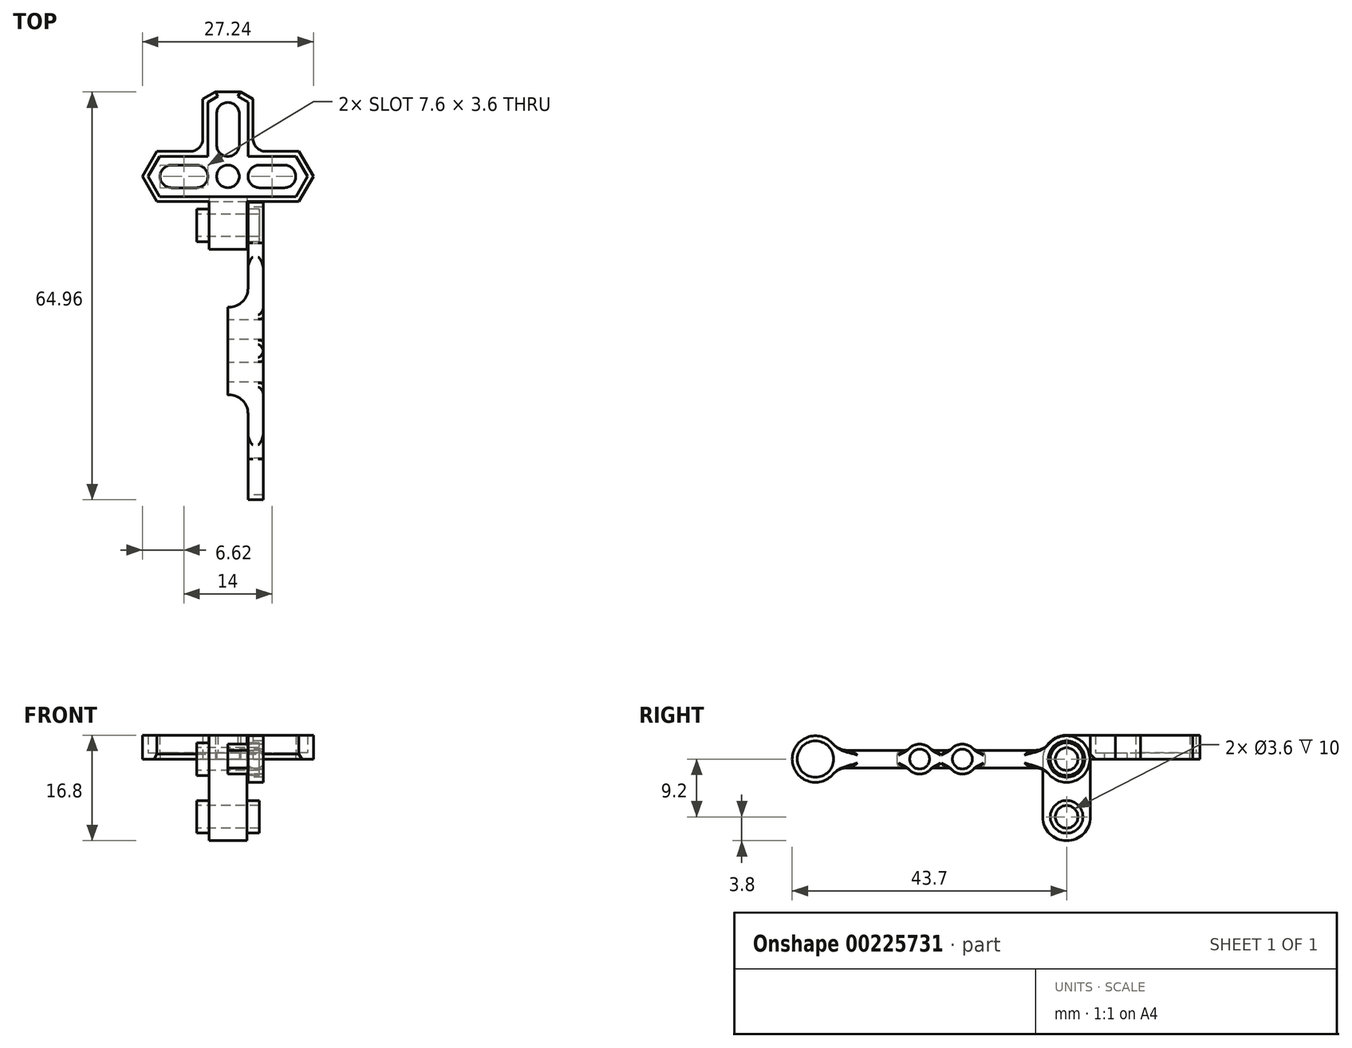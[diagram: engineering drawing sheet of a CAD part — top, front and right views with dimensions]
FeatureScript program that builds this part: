
annotation { "Feature Type Name" : "Feature", "Feature Type Description" : "" }
export const myFeature = defineFeature(function(context is Context, id is Id, definition is map)
    precondition{}
    {
        {
            assignVariable(context, id + "F0", {"name" : "ArmLength", "anyValue" : 40});
        }
        {
            assignVariable(context, id + "F1", {"name" : "OuterArmWidth", "anyValue" : 5.6 * 2});
        }
        {
            assignVariable(context, id + "F2", {"name" : "InnerArmClear", "anyValue" : 6.4});
        }
        {
            var Q0;
            Q0=qCreatedBy(makeId("Front.planeOp"),FACE);
            cPlane(context, id + "F3", {"entities" : qUnion([Q0]), "cplaneType" : CPlaneType.OFFSET, "offset" : (getVariable(context, 'ArmLength') / 2) * mm, "width" : 150 * mm, "height" : 150 * mm});
        }
        {
            var Q0;
            Q0=qCreatedBy(makeId("Right.planeOp"),FACE);
            var sketch = newSketch(context, id + "F4", { "sketchPlane" : qUnion([Q0])});
            skCircle(sketch, "E0", {"center": v(0, 0) * mm, "radius": 2.9 * mm});
            skArc(sketch, "E1", {"start": v(-3.42, -1.4) * mm, "mid": v(3.7, 0) * mm, "end": v(-3.42, 1.4) * mm});
            skCircle(sketch, "E2", {"center": v(-16.6, 0) * mm, "radius": 1.58 * mm});
            skArc(sketch, "E3", {"start": v(-18.52, -1.4) * mm, "mid": v(-16.6, -2.38) * mm, "end": v(-14.68, -1.4) * mm});
            skLineSegment(sketch, "E4", {"start": v(-20, 1.4) * mm, "end": v(-18.52, 1.4) * mm});
            skLineSegment(sketch, "E5", {"start": v(-20, -1.4) * mm, "end": v(-18.52, -1.4) * mm});
            skLineSegment(sketch, "E6", {"start": v(-20, 1.4) * mm, "end": v(-20, -1.4) * mm});
            skLineSegment(sketch, "E7.trimOffspring", {"start": v(-14.68, 1.4) * mm, "end": v(-3.42, 1.4) * mm});
            skLineSegment(sketch, "E8.trimOffspring", {"start": v(-14.68, -1.4) * mm, "end": v(-3.42, -1.4) * mm});
            skArc(sketch, "E9.trimOffspring", {"start": v(-14.68, 1.4) * mm, "mid": v(-16.6, 2.38) * mm, "end": v(-18.52, 1.4) * mm});
            skSolve(sketch);
        }
        {
            var Q0;
            Q0=qCreatedBy(makeId("Right.planeOp"),FACE);
            var sketch = newSketch(context, id + "F5", { "sketchPlane" : qUnion([Q0])});
            skLineSegment(sketch, "E10.bottom", {"start": v(-13, 5) * mm, "end": v(8, 5) * mm});
            skLineSegment(sketch, "E10.top", {"start": v(-13, -5) * mm, "end": v(8, -5) * mm});
            skLineSegment(sketch, "E10.left", {"start": v(-13, 5) * mm, "end": v(-13, -5) * mm});
            skLineSegment(sketch, "E10.right", {"start": v(8, 5) * mm, "end": v(8, -5) * mm});
            skSolve(sketch);
        }
        {
            var Q0;
            Q0=qSketchRegion(id+"F4",true);
            extrude(context, id + "F6", {"entities" : qUnion([Q0]), "depth" : (getVariable(context, 'OuterArmWidth')) / 2 * mm});
        }
        {
            var Q0;
            Q0=qSketchRegion(id+"F5",true);
            extrude(context, id + "F7", {"entities" : qUnion([Q0]), "operationType" : NewBodyOperationType.REMOVE, "depth" : (getVariable(context, 'InnerArmClear')) / 2 * mm});
        }
        {
            var Q0;
            Q0=makeQuery(id+"F6.opExtrude","SWEPT_BODY",BODY,{"disambiguationData":[OSD([sQuery(id+"F4.wireOp",EDGE,"E0"),sQuery(id+"F4.wireOp",EDGE,"E1"),sQuery(id+"F4.wireOp",EDGE,"E2"),sQuery(id+"F4.wireOp",EDGE,"E3"),sQuery(id+"F4.wireOp",EDGE,"E4"),sQuery(id+"F4.wireOp",EDGE,"E5"),sQuery(id+"F4.wireOp",EDGE,"E6"),sQuery(id+"F4.wireOp",EDGE,"E7.trimOffspring"),sQuery(id+"F4.wireOp",EDGE,"E8.trimOffspring"),sQuery(id+"F4.wireOp",EDGE,"E9.trimOffspring")])]});
            var Q1;
            Q1=qCreatedBy(id+"F3.planeOp",FACE);
            mirror(context, id + "F8", {"operationType" : NewBodyOperationType.ADD, "entities" : qUnion([Q0]), "mirrorPlane" : qUnion([Q1])});
        }
        {
            var Q0;
            Q0=makeQuery(id+"F7.boolean.opBoolean","COPY",EDGE,{"derivedFrom":makeQuery(id+"F7.opExtrude","CAP_EDGE",EDGE,{"disambiguationData":[OSD([sQuery(id+"F5.wireOp",EDGE,"E10.left")])],"isStart":false})});
            var Q1;
            Q1=makeQuery(id+"F8.opPattern","COPY",EDGE,{"derivedFrom":makeQuery(id+"F7.boolean.opBoolean","COPY",EDGE,{"derivedFrom":makeQuery(id+"F7.opExtrude","CAP_EDGE",EDGE,{"disambiguationData":[OSD([sQuery(id+"F5.wireOp",EDGE,"E10.left")])],"isStart":false})}),"instanceName":"1"});
            fillet(context, id + "F9", {"entities" : qUnion([Q0, Q1]), "radius" : 3 * mm, "tangentPropagation" : true, "allowEdgeOverflow" : false});
        }
        {
            var Q0;
            Q0=makeQuery(id+"F8.opPattern","COPY",EDGE,{"derivedFrom":makeQuery(id+"F7.boolean.opBoolean","INTERSECT",EDGE,{"derivedFrom":[makeQuery(id+"F6.opExtrude","SWEPT_FACE",FACE,{"disambiguationData":[OSD([sQuery(id+"F4.wireOp",EDGE,"E7.trimOffspring")])]}),makeQuery(id+"F7.opExtrude","CAP_FACE",FACE,{"disambiguationData":[OSD([sQuery(id+"F5.wireOp",EDGE,"E10.bottom"),sQuery(id+"F5.wireOp",EDGE,"E10.top"),sQuery(id+"F5.wireOp",EDGE,"E10.left"),sQuery(id+"F5.wireOp",EDGE,"E10.right")])],"isStart":false})]}),"instanceName":"1"});
            var Q1;
            Q1=makeQuery(id+"F8.opPattern","COPY",EDGE,{"derivedFrom":makeQuery(id+"F7.boolean.opBoolean","INTERSECT",EDGE,{"derivedFrom":[makeQuery(id+"F6.opExtrude","SWEPT_FACE",FACE,{"disambiguationData":[OSD([sQuery(id+"F4.wireOp",EDGE,"E8.trimOffspring")])]}),makeQuery(id+"F7.opExtrude","CAP_FACE",FACE,{"disambiguationData":[OSD([sQuery(id+"F5.wireOp",EDGE,"E10.bottom"),sQuery(id+"F5.wireOp",EDGE,"E10.top"),sQuery(id+"F5.wireOp",EDGE,"E10.left"),sQuery(id+"F5.wireOp",EDGE,"E10.right")])],"isStart":false})]}),"instanceName":"1"});
            var Q2;
            Q2=makeQuery(id+"F8.opPattern","COPY",EDGE,{"derivedFrom":makeQuery(id+"F6.opExtrude","CAP_EDGE",EDGE,{"disambiguationData":[OSD([sQuery(id+"F4.wireOp",EDGE,"E7.trimOffspring")])],"isStart":false}),"instanceName":"1"});
            var Q3;
            {var subQ0=makeQuery(id+"F6.opExtrude","CAP_EDGE",EDGE,{"disambiguationData":[OSD([sQuery(id+"F4.wireOp",EDGE,"E4")])],"isStart":false});Q3=makeQuery(id+"F8.boolean.opBoolean","MERGE",EDGE,{"derivedFrom":[subQ0,makeQuery(id+"F8.opPattern","COPY",EDGE,{"derivedFrom":subQ0,"instanceName":"1"})]});}
            var Q4;
            Q4=makeQuery(id+"F6.opExtrude","CAP_EDGE",EDGE,{"disambiguationData":[OSD([sQuery(id+"F4.wireOp",EDGE,"E7.trimOffspring")])],"isStart":false});
            var Q5;
            Q5=makeQuery(id+"F7.boolean.opBoolean","INTERSECT",EDGE,{"derivedFrom":[makeQuery(id+"F6.opExtrude","SWEPT_FACE",FACE,{"disambiguationData":[OSD([sQuery(id+"F4.wireOp",EDGE,"E7.trimOffspring")])]}),makeQuery(id+"F7.opExtrude","CAP_FACE",FACE,{"disambiguationData":[OSD([sQuery(id+"F5.wireOp",EDGE,"E10.bottom"),sQuery(id+"F5.wireOp",EDGE,"E10.top"),sQuery(id+"F5.wireOp",EDGE,"E10.left"),sQuery(id+"F5.wireOp",EDGE,"E10.right")])],"isStart":false})]});
            var Q6;
            Q6=makeQuery(id+"F7.boolean.opBoolean","INTERSECT",EDGE,{"derivedFrom":[makeQuery(id+"F6.opExtrude","SWEPT_FACE",FACE,{"disambiguationData":[OSD([sQuery(id+"F4.wireOp",EDGE,"E8.trimOffspring")])]}),makeQuery(id+"F7.opExtrude","CAP_FACE",FACE,{"disambiguationData":[OSD([sQuery(id+"F5.wireOp",EDGE,"E10.bottom"),sQuery(id+"F5.wireOp",EDGE,"E10.top"),sQuery(id+"F5.wireOp",EDGE,"E10.left"),sQuery(id+"F5.wireOp",EDGE,"E10.right")])],"isStart":false})]});
            var Q7;
            Q7=makeQuery(id+"F8.opPattern","COPY",EDGE,{"derivedFrom":makeQuery(id+"F6.opExtrude","CAP_EDGE",EDGE,{"disambiguationData":[OSD([sQuery(id+"F4.wireOp",EDGE,"E8.trimOffspring")])],"isStart":false}),"instanceName":"1"});
            var Q8;
            {var subQ0=makeQuery(id+"F6.opExtrude","CAP_EDGE",EDGE,{"disambiguationData":[OSD([sQuery(id+"F4.wireOp",EDGE,"E5")])],"isStart":false});Q8=makeQuery(id+"F8.boolean.opBoolean","MERGE",EDGE,{"derivedFrom":[subQ0,makeQuery(id+"F8.opPattern","COPY",EDGE,{"derivedFrom":subQ0,"instanceName":"1"})]});}
            var Q9;
            Q9=makeQuery(id+"F6.opExtrude","CAP_EDGE",EDGE,{"disambiguationData":[OSD([sQuery(id+"F4.wireOp",EDGE,"E8.trimOffspring")])],"isStart":false});
            fillet(context, id + "F10", {"entities" : qUnion([Q0, Q1, Q2, Q3, Q4, Q5, Q6, Q7, Q8, Q9]), "radius" : 0.8 * mm, "tangentPropagation" : true, "allowEdgeOverflow" : false});
        }
        {
            var Q0;
            Q0=makeQuery(id+"F8.opPattern","COPY",EDGE,{"derivedFrom":makeQuery(id+"F6.opExtrude","SWEPT_EDGE",EDGE,{"disambiguationData":[OSD([sQuery(id+"F4.wireOp",EDGE,"E1"),sQuery(id+"F4.wireOp",EDGE,"E8.trimOffspring")])]}),"instanceName":"1"});
            var Q1;
            Q1=makeQuery(id+"F10.opFillet","BLEND_EDGE",EDGE,{"blendedFrom":[makeQuery(id+"F8.opPattern","COPY",EDGE,{"derivedFrom":makeQuery(id+"F6.opExtrude","CAP_EDGE",EDGE,{"disambiguationData":[OSD([sQuery(id+"F4.wireOp",EDGE,"E7.trimOffspring")])],"isStart":false}),"instanceName":"1"}),makeQuery(id+"F8.opPattern","COPY",FACE,{"derivedFrom":makeQuery(id+"F6.opExtrude","SWEPT_FACE",FACE,{"disambiguationData":[OSD([sQuery(id+"F4.wireOp",EDGE,"E1")])]}),"instanceName":"1"})],"blendedInto":[makeQuery(id+"F8.opPattern","COPY",FACE,{"derivedFrom":makeQuery(id+"F6.opExtrude","SWEPT_FACE",FACE,{"disambiguationData":[OSD([sQuery(id+"F4.wireOp",EDGE,"E1")])]}),"instanceName":"1"})]});
            var Q2;
            Q2=makeQuery(id+"F6.opExtrude","SWEPT_EDGE",EDGE,{"disambiguationData":[OSD([sQuery(id+"F4.wireOp",EDGE,"E1"),sQuery(id+"F4.wireOp",EDGE,"E7.trimOffspring")])]});
            var Q3;
            Q3=makeQuery(id+"F6.opExtrude","SWEPT_EDGE",EDGE,{"disambiguationData":[OSD([sQuery(id+"F4.wireOp",EDGE,"E1"),sQuery(id+"F4.wireOp",EDGE,"E8.trimOffspring")])]});
            fillet(context, id + "F11", {"entities" : qUnion([Q0, Q1, Q2, Q3]), "radius" : 3 * mm, "tangentPropagation" : true, "allowEdgeOverflow" : false});
        }
        {
            var Q0;
            Q0=makeQuery(id+"F6.opExtrude","SWEPT_EDGE",EDGE,{"disambiguationData":[OSD([sQuery(id+"F4.wireOp",EDGE,"E3"),sQuery(id+"F4.wireOp",EDGE,"E8.trimOffspring")])]});
            var Q1;
            Q1=makeQuery(id+"F6.opExtrude","SWEPT_EDGE",EDGE,{"disambiguationData":[OSD([sQuery(id+"F4.wireOp",EDGE,"E3"),sQuery(id+"F4.wireOp",EDGE,"E5")])]});
            var Q2;
            Q2=makeQuery(id+"F8.opPattern","COPY",EDGE,{"derivedFrom":makeQuery(id+"F6.opExtrude","SWEPT_EDGE",EDGE,{"disambiguationData":[OSD([sQuery(id+"F4.wireOp",EDGE,"E3"),sQuery(id+"F4.wireOp",EDGE,"E5")])]}),"instanceName":"1"});
            var Q3;
            Q3=makeQuery(id+"F8.opPattern","COPY",EDGE,{"derivedFrom":makeQuery(id+"F6.opExtrude","SWEPT_EDGE",EDGE,{"disambiguationData":[OSD([sQuery(id+"F4.wireOp",EDGE,"E3"),sQuery(id+"F4.wireOp",EDGE,"E8.trimOffspring")])]}),"instanceName":"1"});
            var Q4;
            Q4=makeQuery(id+"F6.opExtrude","SWEPT_EDGE",EDGE,{"disambiguationData":[OSD([sQuery(id+"F4.wireOp",EDGE,"E7.trimOffspring"),sQuery(id+"F4.wireOp",EDGE,"E9.trimOffspring")])]});
            var Q5;
            Q5=makeQuery(id+"F6.opExtrude","SWEPT_EDGE",EDGE,{"disambiguationData":[OSD([sQuery(id+"F4.wireOp",EDGE,"E4"),sQuery(id+"F4.wireOp",EDGE,"E9.trimOffspring")])]});
            var Q6;
            Q6=makeQuery(id+"F8.opPattern","COPY",EDGE,{"derivedFrom":makeQuery(id+"F6.opExtrude","SWEPT_EDGE",EDGE,{"disambiguationData":[OSD([sQuery(id+"F4.wireOp",EDGE,"E4"),sQuery(id+"F4.wireOp",EDGE,"E9.trimOffspring")])]}),"instanceName":"1"});
            var Q7;
            Q7=makeQuery(id+"F8.opPattern","COPY",EDGE,{"derivedFrom":makeQuery(id+"F6.opExtrude","SWEPT_EDGE",EDGE,{"disambiguationData":[OSD([sQuery(id+"F4.wireOp",EDGE,"E7.trimOffspring"),sQuery(id+"F4.wireOp",EDGE,"E9.trimOffspring")])]}),"instanceName":"1"});
            fillet(context, id + "F12", {"entities" : qUnion([Q0, Q1, Q2, Q3, Q4, Q5, Q6, Q7]), "radius" : 1 * mm, "tangentPropagation" : true, "allowEdgeOverflow" : false});
        }
        {
            var Q0;
            Q0=qCreatedBy(makeId("Right.planeOp"),FACE);
            var sketch = newSketch(context, id + "F13", { "sketchPlane" : qUnion([Q0])});
            skCircle(sketch, "E11", {"center": v(0, 0) * mm, "radius": 1.8 * mm});
            skCircle(sketch, "E12", {"center": v(0, -9.2) * mm, "radius": 1.8 * mm});
            skCircle(sketch, "E13", {"center": v(0, 0) * mm, "radius": 2.6 * mm});
            skCircle(sketch, "E14", {"center": v(0, -9.2) * mm, "radius": 2.6 * mm});
            skArc(sketch, "E15", {"start": v(-3.8, -9.2) * mm, "mid": v(0, -13) * mm, "end": v(3.8, -9.2) * mm});
            skArc(sketch, "E16", {"start": v(0, 3.8) * mm, "mid": v(-2.69, 2.69) * mm, "end": v(-3.8, 0) * mm});
            skLineSegment(sketch, "E17", {"start": v(-3.8, 0) * mm, "end": v(-3.8, -9.2) * mm});
            skLineSegment(sketch, "E18", {"start": v(3.8, 3.8) * mm, "end": v(3.8, -9.2) * mm});
            skLineSegment(sketch, "E19", {"start": v(0, 3.8) * mm, "end": v(3.8, 3.8) * mm});
            skSolve(sketch);
        }
        {
            var Q0;
            Q0=qCreatedBy(makeId("Right.planeOp"),FACE);
            var sketch = newSketch(context, id + "F14", { "sketchPlane" : qUnion([Q0])});
            skLineSegment(sketch, "E20.0", {"start": v(0, 3.8) * mm, "end": v(3.8, 3.8) * mm});
            skArc(sketch, "E20.1", {"start": v(0, 3.8) * mm, "mid": v(-2.69, 2.69) * mm, "end": v(-3.8, 0) * mm});
            skLineSegment(sketch, "E20.2", {"start": v(-3.8, 0) * mm, "end": v(-3.8, -9.2) * mm});
            skArc(sketch, "E20.3", {"start": v(-3.8, -9.2) * mm, "mid": v(0, -13) * mm, "end": v(3.8, -9.2) * mm});
            skLineSegment(sketch, "E20.4", {"start": v(3.8, 3.8) * mm, "end": v(3.8, -9.2) * mm});
            skCircle(sketch, "E20.5", {"center": v(0, 0) * mm, "radius": 1.8 * mm});
            skCircle(sketch, "E20.6", {"center": v(0, -9.2) * mm, "radius": 1.8 * mm});
            skSolve(sketch);
        }
        {
            var Q0;
            Q0=qSketchRegion(id+"F14",true);
            extrude(context, id + "F15", {"entities" : qUnion([Q0]), "endBound" : BoundingType.SYMMETRIC, "depth" : ((getVariable(context, 'InnerArmClear')) - 0.4) * mm});
        }
        {
            var Q0;
            Q0=qCreatedBy(makeId("Right.planeOp"),FACE);
            var sketch = newSketch(context, id + "F16", { "sketchPlane" : qUnion([Q0])});
            skCircle(sketch, "E21.0", {"center": v(0, 0) * mm, "radius": 2.6 * mm});
            skCircle(sketch, "E21.1", {"center": v(0, 0) * mm, "radius": 1.8 * mm});
            skCircle(sketch, "E22.0", {"center": v(0, -9.2) * mm, "radius": 2.6 * mm});
            skCircle(sketch, "E22.1", {"center": v(0, -9.2) * mm, "radius": 1.8 * mm});
            skSolve(sketch);
        }
        {
            var Q0;
            Q0=qSketchRegion(id+"F16",true);
            extrude(context, id + "F17", {"entities" : qUnion([Q0]), "operationType" : NewBodyOperationType.ADD, "endBound" : BoundingType.SYMMETRIC, "depth" : 10 * mm});
        }
        {
            var Q0;
            Q0=qCreatedBy(makeId("Top.planeOp"),FACE);
            var sketch = newSketch(context, id + "F18", { "sketchPlane" : qUnion([Q0])});
            skCircle(sketch, "E23", {"center": v(0, 7.8) * mm, "radius": 1.8 * mm});
            skArc(sketch, "E24", {"start": v(1.8, 17.8) * mm, "mid": v(0, 19.6) * mm, "end": v(-1.8, 17.8) * mm});
            skArc(sketch, "E25", {"start": v(-1.8, 12.8) * mm, "mid": v(0, 11) * mm, "end": v(1.8, 12.8) * mm});
            skLineSegment(sketch, "E26", {"start": v(-1.8, 17.8) * mm, "end": v(-1.8, 12.8) * mm});
            skLineSegment(sketch, "E27", {"start": v(1.8, 17.8) * mm, "end": v(1.8, 12.8) * mm});
            skLineSegment(sketch, "E28", {"start": v(0, 7.8) * mm, "end": v(-9, 7.8) * mm, "construction": true});
            skArc(sketch, "E29", {"start": v(-9, 9.6) * mm, "mid": v(-10.8, 7.8) * mm, "end": v(-9, 6) * mm});
            skLineSegment(sketch, "E30", {"start": v(0, 7.8) * mm, "end": v(9, 7.8) * mm, "construction": true});
            skArc(sketch, "E31", {"start": v(9, 6) * mm, "mid": v(10.8, 7.8) * mm, "end": v(9, 9.6) * mm});
            skLineSegment(sketch, "E32", {"start": v(-11.3, 3.8) * mm, "end": v(11.3, 3.8) * mm});
            skArc(sketch, "E33", {"start": v(-5, 6) * mm, "mid": v(-3.2, 7.8) * mm, "end": v(-5, 9.6) * mm});
            skArc(sketch, "E34", {"start": v(5, 9.6) * mm, "mid": v(3.2, 7.8) * mm, "end": v(5, 6) * mm});
            skLineSegment(sketch, "E35", {"start": v(-9, 9.6) * mm, "end": v(-5, 9.6) * mm});
            skLineSegment(sketch, "E36", {"start": v(-9, 6) * mm, "end": v(-5, 6) * mm});
            skLineSegment(sketch, "E37", {"start": v(5, 9.6) * mm, "end": v(9, 9.6) * mm});
            skLineSegment(sketch, "E38", {"start": v(5, 6) * mm, "end": v(9, 6) * mm});
            skCircle(sketch, "E39.cCircle", {"center": v(-9, 7.8) * mm, "radius": 4 * mm, "construction": true});
            skLineSegment(sketch, "E39.0", {"start": v(-6.7, 3.8) * mm, "end": v(-11.3, 3.8) * mm, "construction": true});
            skLineSegment(sketch, "E39.1", {"start": v(-11.3, 3.8) * mm, "end": v(-13.62, 7.8) * mm});
            skLineSegment(sketch, "E39.2", {"start": v(-13.62, 7.8) * mm, "end": v(-11.3, 11.8) * mm});
            skLineSegment(sketch, "E39.3", {"start": v(-11.3, 11.8) * mm, "end": v(-6.7, 11.8) * mm});
            skLineSegment(sketch, "E39.4", {"start": v(-6.7, 11.8) * mm, "end": v(-4.38, 7.8) * mm, "construction": true});
            skLineSegment(sketch, "E39.5", {"start": v(-4.38, 7.8) * mm, "end": v(-6.7, 3.8) * mm, "construction": true});
            skPoint(sketch, "E39.0.midPoint", {"position": v(-9, 3.8) * mm});
            skPoint(sketch, "E40.orphan", {"position": v(-13.62, 7.8) * mm});
            skCircle(sketch, "E41.cCircle", {"center": v(0, 17.8) * mm, "radius": 4 * mm, "construction": true});
            skLineSegment(sketch, "E41.0", {"start": v(-4, 15.5) * mm, "end": v(-4, 20.1) * mm});
            skLineSegment(sketch, "E41.1", {"start": v(-4, 20.1) * mm, "end": v(-2, 21.26) * mm});
            skLineSegment(sketch, "E41.2", {"start": v(2, 21.26) * mm, "end": v(4, 20.1) * mm});
            skLineSegment(sketch, "E41.3", {"start": v(4, 20.1) * mm, "end": v(4, 15.5) * mm});
            skLineSegment(sketch, "E41.4", {"start": v(4, 15.5) * mm, "end": v(0, 13.18) * mm, "construction": true});
            skLineSegment(sketch, "E41.5", {"start": v(0, 13.18) * mm, "end": v(-4, 15.5) * mm, "construction": true});
            skPoint(sketch, "E41.0.midPoint", {"position": v(-4, 17.8) * mm});
            skLineSegment(sketch, "E42", {"start": v(-2, 21.26) * mm, "end": v(2, 21.26) * mm});
            skPoint(sketch, "E43.orphan", {"position": v(0, 22.42) * mm});
            skLineSegment(sketch, "E44", {"start": v(-4, 15.5) * mm, "end": v(-4, 11.8) * mm});
            skLineSegment(sketch, "E45", {"start": v(-4, 11.8) * mm, "end": v(-6.7, 11.8) * mm});
            skCircle(sketch, "E46.cCircle", {"center": v(9, 7.8) * mm, "radius": 4 * mm, "construction": true});
            skLineSegment(sketch, "E46.0", {"start": v(11.3, 3.8) * mm, "end": v(6.7, 3.8) * mm, "construction": true});
            skLineSegment(sketch, "E46.1", {"start": v(6.7, 3.8) * mm, "end": v(4.38, 7.8) * mm, "construction": true});
            skLineSegment(sketch, "E46.2", {"start": v(4.38, 7.8) * mm, "end": v(6.7, 11.8) * mm, "construction": true});
            skLineSegment(sketch, "E46.3", {"start": v(6.7, 11.8) * mm, "end": v(11.3, 11.8) * mm});
            skLineSegment(sketch, "E46.4", {"start": v(11.3, 11.8) * mm, "end": v(13.62, 7.8) * mm});
            skLineSegment(sketch, "E46.5", {"start": v(13.62, 7.8) * mm, "end": v(11.3, 3.8) * mm});
            skPoint(sketch, "E46.0.midPoint", {"position": v(9, 3.8) * mm});
            skPoint(sketch, "E47.orphan", {"position": v(13.62, 7.8) * mm});
            skLineSegment(sketch, "E48", {"start": v(4, 15.5) * mm, "end": v(4, 11.8) * mm});
            skLineSegment(sketch, "E49", {"start": v(4, 11.8) * mm, "end": v(6.7, 11.8) * mm});
            skPoint(sketch, "E50.orphan", {"position": v(-12.46, 9.8) * mm});
            skPoint(sketch, "E51.orphan", {"position": v(-12.46, 5.8) * mm});
            skPoint(sketch, "E52.orphan", {"position": v(12.46, 5.8) * mm});
            skPoint(sketch, "E53.orphan", {"position": v(12.46, 9.8) * mm});
            skSolve(sketch);
        }
        {
            var Q0;
            Q0=qSketchRegion(id+"F18",true);
            var Q1;
            Q1=makeQuery(id+"F15.opExtrude","SWEPT_FACE",FACE,{"disambiguationData":[OSD([sQuery(id+"F14.wireOp",EDGE,"E20.0")])]});
            extrude(context, id + "F19", {"entities" : qUnion([Q0]), "operationType" : NewBodyOperationType.ADD, "endBound" : BoundingType.UP_TO_SURFACE, "endBoundEntityFace" : qUnion([Q1]), "depth" : 25 * mm});
        }
        {
            var Q0;
            Q0=qCreatedBy(makeId("Top.planeOp"),FACE);
            var sketch = newSketch(context, id + "F20", { "sketchPlane" : qUnion([Q0])});
            skLineSegment(sketch, "E54.0", {"start": v(-10.85, 4.6) * mm, "end": v(-3, 4.6) * mm});
            skLineSegment(sketch, "E54.1", {"start": v(-10.85, 4.6) * mm, "end": v(-12.7, 7.8) * mm});
            skLineSegment(sketch, "E54.3", {"start": v(-12.7, 7.8) * mm, "end": v(-10.85, 11) * mm});
            skLineSegment(sketch, "E54.4", {"start": v(-3.2, 11) * mm, "end": v(-10.85, 11) * mm});
            skLineSegment(sketch, "E54.5", {"start": v(10.85, 11) * mm, "end": v(12.7, 7.8) * mm});
            skLineSegment(sketch, "E54.7", {"start": v(12.7, 7.8) * mm, "end": v(10.85, 4.6) * mm});
            skLineSegment(sketch, "E54.8", {"start": v(3, 4.6) * mm, "end": v(10.85, 4.6) * mm});
            skLineSegment(sketch, "E54.9", {"start": v(3.2, 11) * mm, "end": v(10.85, 11) * mm});
            skLineSegment(sketch, "E54.10", {"start": v(3.2, 19.65) * mm, "end": v(3.2, 11) * mm});
            skLineSegment(sketch, "E54.11", {"start": v(1.6, 20.57) * mm, "end": v(3.2, 19.65) * mm});
            skLineSegment(sketch, "E54.13", {"start": v(-3.2, 19.65) * mm, "end": v(-1.6, 20.57) * mm});
            skLineSegment(sketch, "E54.14", {"start": v(-3.2, 11) * mm, "end": v(-3.2, 19.65) * mm});
            skLineSegment(sketch, "E55.0", {"start": v(-2, 21.26) * mm, "end": v(2, 21.26) * mm});
            skLineSegment(sketch, "E56", {"start": v(-1.6, 20.57) * mm, "end": v(-2, 21.26) * mm});
            skLineSegment(sketch, "E57", {"start": v(1.6, 20.57) * mm, "end": v(2, 21.26) * mm});
            skLineSegment(sketch, "E58", {"start": v(-3, 4.6) * mm, "end": v(3, 4.6) * mm});
            skSolve(sketch);
        }
        {
            var Q0;
            Q0=qSketchRegion(id+"F20",true);
            extrude(context, id + "F21", {"entities" : qUnion([Q0]), "operationType" : NewBodyOperationType.REMOVE, "endBound" : BoundingType.THROUGH_ALL, "depth" : 25 * mm, "hasSecondDirection" : true, "secondDirectionOppositeDirection" : false, "secondDirectionDepth" : 1 * mm});
        }
        {
            var Q0;
            Q0=makeQuery(id+"F19.opExtrude","SWEPT_EDGE",EDGE,{"disambiguationData":[OSD([sQuery(id+"F18.wireOp",EDGE,"E48"),sQuery(id+"F18.wireOp",EDGE,"E49")])]});
            var Q1;
            Q1=makeQuery(id+"F19.opExtrude","SWEPT_EDGE",EDGE,{"disambiguationData":[OSD([sQuery(id+"F18.wireOp",EDGE,"E44"),sQuery(id+"F18.wireOp",EDGE,"E45")])]});
            fillet(context, id + "F22", {"entities" : qUnion([Q0, Q1]), "radius" : 2 * mm, "tangentPropagation" : true, "allowEdgeOverflow" : false});
        }
        {
            var Q0;
            {var subQ0=sQuery(id+"F18.wireOp",EDGE,"E32");Q0=makeQuery(id+"F19.boolean.opBoolean","SPLIT",EDGE,{"disambiguationData":[topologyDisambiguationEdgeConnected([makeQuery(id+"F15.opExtrude","SWEPT_FACE",FACE,{"disambiguationData":[OSD([sQuery(id+"F14.wireOp",EDGE,"E20.4")])]}),makeQuery(id+"F19.opExtrude","CAP_FACE",FACE,{"disambiguationData":[OSD([sQuery(id+"F18.wireOp",EDGE,"E23"),sQuery(id+"F18.wireOp",EDGE,"E24"),sQuery(id+"F18.wireOp",EDGE,"E25"),sQuery(id+"F18.wireOp",EDGE,"E26"),sQuery(id+"F18.wireOp",EDGE,"E27"),sQuery(id+"F18.wireOp",EDGE,"E29"),sQuery(id+"F18.wireOp",EDGE,"E31"),subQ0,sQuery(id+"F18.wireOp",EDGE,"E33"),sQuery(id+"F18.wireOp",EDGE,"E34"),sQuery(id+"F18.wireOp",EDGE,"E35"),sQuery(id+"F18.wireOp",EDGE,"E36"),sQuery(id+"F18.wireOp",EDGE,"E37"),sQuery(id+"F18.wireOp",EDGE,"E38"),sQuery(id+"F18.wireOp",EDGE,"E39.1"),sQuery(id+"F18.wireOp",EDGE,"E39.2"),sQuery(id+"F18.wireOp",EDGE,"E39.3"),sQuery(id+"F18.wireOp",EDGE,"E41.0"),sQuery(id+"F18.wireOp",EDGE,"E41.1"),sQuery(id+"F18.wireOp",EDGE,"E41.2"),sQuery(id+"F18.wireOp",EDGE,"E41.3"),sQuery(id+"F18.wireOp",EDGE,"E42"),sQuery(id+"F18.wireOp",EDGE,"E44"),sQuery(id+"F18.wireOp",EDGE,"E45"),sQuery(id+"F18.wireOp",EDGE,"E46.3"),sQuery(id+"F18.wireOp",EDGE,"E46.4"),sQuery(id+"F18.wireOp",EDGE,"E46.5"),sQuery(id+"F18.wireOp",EDGE,"E48"),sQuery(id+"F18.wireOp",EDGE,"E49")])],"isStart":true})])],"derivedFrom":makeQuery(id+"F19.opExtrude","CAP_EDGE",EDGE,{"disambiguationData":[OSD([subQ0])],"isStart":true})});}
            chamfer(context, id + "F23", {"entities" : qUnion([Q0]), "width" : 0.8 * mm, "tangentPropagation" : true});
        }
    });
